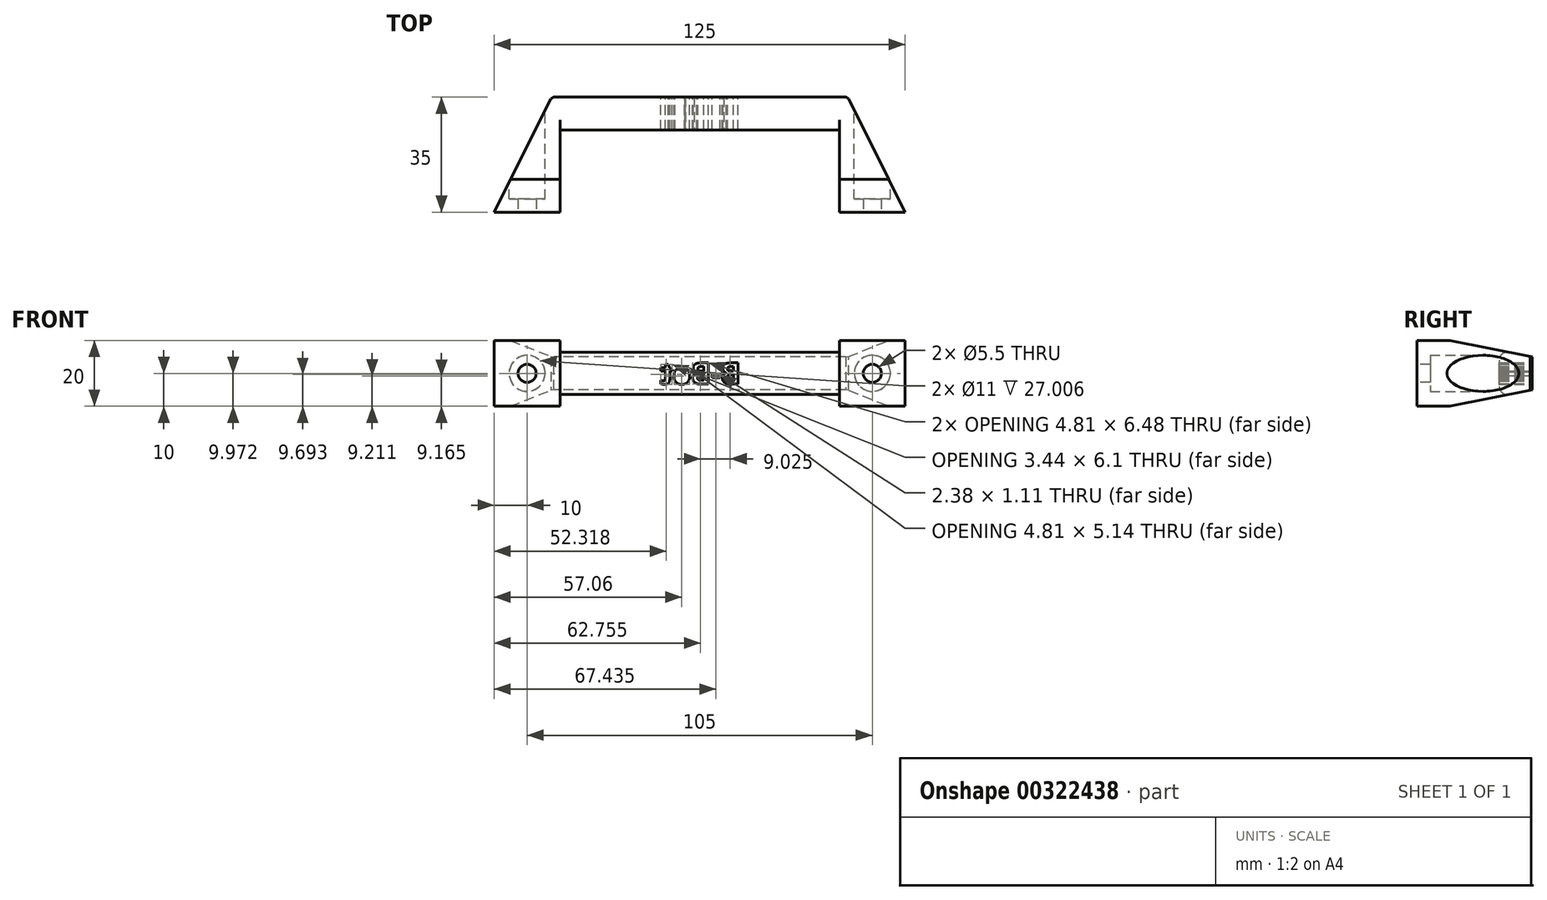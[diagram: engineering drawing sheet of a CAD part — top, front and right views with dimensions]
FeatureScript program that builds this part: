
annotation { "Feature Type Name" : "Feature", "Feature Type Description" : "" }
export const myFeature = defineFeature(function(context is Context, id is Id, definition is map)
    precondition{}
    {
        {
            var Q0;
            Q0=qCreatedBy(makeId("Top.planeOp"),FACE);
            var sketch = newSketch(context, id + "F0", { "sketchPlane" : qUnion([Q0])});
            skLineSegment(sketch, "E0", {"start": v(0, 0) * mm, "end": v(-20, 0) * mm});
            skLineSegment(sketch, "E1", {"start": v(0, 0) * mm, "end": v(0, 25) * mm});
            skLineSegment(sketch, "E2", {"start": v(0, 25) * mm, "end": v(85, 25) * mm});
            skLineSegment(sketch, "E3", {"start": v(85, 25) * mm, "end": v(85, 0) * mm});
            skLineSegment(sketch, "E4", {"start": v(85, 0) * mm, "end": v(105, 0) * mm});
            skLineSegment(sketch, "E5", {"start": v(105, 0) * mm, "end": v(87.5, 35) * mm});
            skLineSegment(sketch, "E6", {"start": v(87.5, 35) * mm, "end": v(-2.5, 35) * mm});
            skLineSegment(sketch, "E7", {"start": v(-2.5, 35) * mm, "end": v(-20, 0) * mm});
            skSolve(sketch);
        }
        {
            var Q0;
            Q0=makeQuery(id+"F0.imprint","IMPRINT",FACE,{"disambiguationData":[TD([[makeQuery(id+"F0.imprint","IMPRINT",EDGE,{"derivedFrom":sQuery(id+"F0.wireOp",EDGE,"E0")}),-1.0]])]});
            extrude(context, id + "F1", {"entities" : qUnion([Q0]), "depth" : 20 * mm});
        }
        {
            var Q0;
            Q0=qCreatedBy(makeId("Right.planeOp"),FACE);
            cPlane(context, id + "F2", {"entities" : qUnion([Q0]), "cplaneType" : CPlaneType.OFFSET, "offset" : 20 * mm, "oppositeDirection" : true, "width" : 150 * mm, "height" : 150 * mm});
        }
        {
            var Q0;
            Q0=qCreatedBy(id+"F2.planeOp",FACE);
            var sketch = newSketch(context, id + "F3", { "sketchPlane" : qUnion([Q0])});
            skLineSegment(sketch, "E8.0.0", {"start": v(35, 0) * mm, "end": v(0, 0) * mm, "construction": true});
            skLineSegment(sketch, "E8.0.1", {"start": v(0, 0) * mm, "end": v(0, 20) * mm, "construction": true});
            skLineSegment(sketch, "E8.0.2", {"start": v(0, 20) * mm, "end": v(35, 20) * mm, "construction": true});
            skLineSegment(sketch, "E8.0.3", {"start": v(35, 20) * mm, "end": v(35, 0) * mm, "construction": true});
            skLineSegment(sketch, "E9.0.1", {"start": v(25, 0) * mm, "end": v(25, 20) * mm, "construction": true});
            skLineSegment(sketch, "E9.0.3", {"start": v(25, 20) * mm, "end": v(25, 0) * mm, "construction": true});
            skLineSegment(sketch, "E10", {"start": v(35, 5) * mm, "end": v(10, 0) * mm});
            skLineSegment(sketch, "E11", {"start": v(10, 0) * mm, "end": v(35, 0) * mm});
            skLineSegment(sketch, "E12", {"start": v(35, 0) * mm, "end": v(35, 5) * mm});
            skLineSegment(sketch, "E13", {"start": v(35, 10) * mm, "end": v(0, 10) * mm, "construction": true});
            skLineSegment(sketch, "E14.MirrorCS", {"start": v(10, 20) * mm, "end": v(35, 20) * mm});
            skLineSegment(sketch, "E15.MirrorCS", {"start": v(35, 15) * mm, "end": v(10, 20) * mm});
            skLineSegment(sketch, "E16.MirrorCS", {"start": v(35, 20) * mm, "end": v(35, 15) * mm});
            skSolve(sketch);
        }
        {
            var Q0;
            Q0 = qSketchRegion(id + "F3", true);
            extrude(context, id + "F4", {"entities" : qUnion([Q0]), "operationType" : NewBodyOperationType.REMOVE, "endBound" : BoundingType.THROUGH_ALL, "depth" : 25 * mm});
        }
        {
            var Q0;
            Q0=makeQuery(id+"F1.opExtrude","SWEPT_FACE",FACE,{"disambiguationData":[OSD([sQuery(id+"F0.wireOp",EDGE,"E6")])]});
            var sketch = newSketch(context, id + "F5", { "sketchPlane" : qUnion([Q0])});
            skLineSegment(sketch, "E17.0.0", {"start": v(-87.5, 15) * mm, "end": v(-87.5, 5) * mm, "construction": true});
            skLineSegment(sketch, "E17.0.1", {"start": v(-87.5, 5) * mm, "end": v(2.5, 5) * mm, "construction": true});
            skLineSegment(sketch, "E17.0.2", {"start": v(2.5, 5) * mm, "end": v(2.5, 15) * mm, "construction": true});
            skLineSegment(sketch, "E17.0.3", {"start": v(2.5, 15) * mm, "end": v(-87.5, 15) * mm, "construction": true});
            skText(sketch, "E18", { "text": "B-Bot", "fontName": "OpenSans-Bold.ttf"});
            const initialGuessF5  = {"E18": [-0.055, 0.00673, 1, 0, 0.00654]};
            skSetInitialGuess(sketch, initialGuessF5);
            skSolve(sketch);
        }
        {
            var Q0;
            Q0 = qSketchRegion(id + "F5", true);
            extrude(context, id + "F6", {"entities" : qUnion([Q0]), "operationType" : NewBodyOperationType.REMOVE, "endBound" : BoundingType.THROUGH_ALL, "oppositeDirection" : true, "depth" : 25 * mm});
        }
        {
            var Q0;
            Q0=makeQuery(id+"F6.boolean.opBoolean","SPLIT",FACE,{"disambiguationData":[TD([makeQuery(id+"F1.opExtrude","SWEPT_FACE",FACE,{"disambiguationData":[OSD([sQuery(id+"F0.wireOp",EDGE,"E5")])]})])],"derivedFrom":makeQuery(id+"F1.opExtrude","SWEPT_FACE",FACE,{"disambiguationData":[OSD([sQuery(id+"F0.wireOp",EDGE,"E6")])]})});
            var sketch = newSketch(context, id + "F7", { "sketchPlane" : qUnion([Q0])});
            skLineSegment(sketch, "E19.0.0", {"start": v(-50.3, 12.09) * mm, "end": v(-50.3, 10.65) * mm});
            skLineSegment(sketch, "E19.0.1", {"start": v(-50.3, 10.65) * mm, "end": v(-49.51, 10.65) * mm});
            skFitSpline(sketch, "E19.0.2", {"points": [v(-52.01, 10.65) * mm, v(-51.45, 10.65) * mm, v(-51.2, 10.82) * mm]});
            skFitSpline(sketch, "E19.0.3", {"points": [v(-51.2, 10.82) * mm, v(-50.95, 11) * mm, v(-50.95, 11.4) * mm]});
            skFitSpline(sketch, "E19.0.4", {"points": [v(-50.95, 11.4) * mm, v(-50.95, 11.76) * mm, v(-51.22, 11.93) * mm]});
            skFitSpline(sketch, "E19.0.5", {"points": [v(-51.22, 11.93) * mm, v(-51.5, 12.09) * mm, v(-52.09, 12.09) * mm]});
            skLineSegment(sketch, "E19.0.6", {"start": v(-49.59, 12.09) * mm, "end": v(-50.3, 12.09) * mm});
            skLineSegment(sketch, "E20.0.0", {"start": v(-49.46, 9.56) * mm, "end": v(-50.3, 9.56) * mm});
            skLineSegment(sketch, "E20.0.1", {"start": v(-50.3, 9.56) * mm, "end": v(-50.3, 7.86) * mm});
            skLineSegment(sketch, "E20.0.2", {"start": v(-50.3, 7.86) * mm, "end": v(-49.41, 7.86) * mm});
            skFitSpline(sketch, "E20.0.3", {"points": [v(-51.91, 7.86) * mm, v(-51.34, 7.86) * mm, v(-51.07, 8.08) * mm]});
            skFitSpline(sketch, "E20.0.4", {"points": [v(-51.07, 8.08) * mm, v(-50.8, 8.3) * mm, v(-50.8, 8.75) * mm]});
            skFitSpline(sketch, "E20.0.5", {"points": [v(-50.8, 8.75) * mm, v(-50.8, 9.56) * mm, v(-51.96, 9.56) * mm]});
            skLineSegment(sketch, "E21.0.0", {"start": v(-41.28, 12.09) * mm, "end": v(-41.28, 10.65) * mm});
            skLineSegment(sketch, "E21.0.1", {"start": v(-41.28, 10.65) * mm, "end": v(-40.48, 10.65) * mm});
            skFitSpline(sketch, "E21.0.2", {"points": [v(-42.98, 10.65) * mm, v(-42.42, 10.65) * mm, v(-42.17, 10.82) * mm]});
            skFitSpline(sketch, "E21.0.3", {"points": [v(-42.17, 10.82) * mm, v(-41.92, 11) * mm, v(-41.92, 11.4) * mm]});
            skFitSpline(sketch, "E21.0.4", {"points": [v(-41.92, 11.4) * mm, v(-41.92, 11.76) * mm, v(-42.2, 11.93) * mm]});
            skFitSpline(sketch, "E21.0.5", {"points": [v(-42.2, 11.93) * mm, v(-42.47, 12.09) * mm, v(-43.06, 12.09) * mm]});
            skLineSegment(sketch, "E21.0.6", {"start": v(-40.56, 12.09) * mm, "end": v(-41.28, 12.09) * mm});
            skLineSegment(sketch, "E22.0.0", {"start": v(-40.43, 9.56) * mm, "end": v(-41.28, 9.56) * mm});
            skLineSegment(sketch, "E22.0.1", {"start": v(-41.28, 9.56) * mm, "end": v(-41.28, 7.86) * mm});
            skLineSegment(sketch, "E22.0.2", {"start": v(-41.28, 7.86) * mm, "end": v(-40.38, 7.86) * mm});
            skFitSpline(sketch, "E22.0.3", {"points": [v(-42.88, 7.86) * mm, v(-42.32, 7.86) * mm, v(-42.05, 8.08) * mm]});
            skFitSpline(sketch, "E22.0.4", {"points": [v(-42.05, 8.08) * mm, v(-41.78, 8.3) * mm, v(-41.78, 8.75) * mm]});
            skFitSpline(sketch, "E22.0.5", {"points": [v(-41.78, 8.75) * mm, v(-41.78, 9.56) * mm, v(-42.93, 9.56) * mm]});
            skFitSpline(sketch, "E23.0.0", {"points": [v(-37.84, 10.33) * mm, v(-38.08, 9.96) * mm, v(-38.08, 9.22) * mm]});
            skFitSpline(sketch, "E23.0.1", {"points": [v(-38.08, 9.22) * mm, v(-38.08, 8.48) * mm, v(-37.84, 8.1) * mm]});
            skFitSpline(sketch, "E23.0.2", {"points": [v(-37.84, 8.1) * mm, v(-37.6, 7.73) * mm, v(-37.05, 7.73) * mm]});
            skFitSpline(sketch, "E23.0.3", {"points": [v(-37.05, 7.73) * mm, v(-36.5, 7.73) * mm, v(-36.27, 8.1) * mm]});
            skFitSpline(sketch, "E23.0.4", {"points": [v(-36.27, 8.1) * mm, v(-36.03, 8.48) * mm, v(-36.03, 9.22) * mm]});
            skFitSpline(sketch, "E23.0.5", {"points": [v(-36.03, 9.22) * mm, v(-36.03, 9.95) * mm, v(-36.27, 10.32) * mm]});
            skFitSpline(sketch, "E23.0.6", {"points": [v(-36.27, 10.32) * mm, v(-36.51, 10.7) * mm, v(-37.06, 10.7) * mm]});
            skFitSpline(sketch, "E23.0.7", {"points": [v(-37.06, 10.7) * mm, v(-37.6, 10.7) * mm, v(-37.84, 10.33) * mm]});
            skSolve(sketch);
        }
        {
            var Q0;
            Q0 = qSketchRegion(id + "F7", true);
            extrude(context, id + "F8", {"entities" : qUnion([Q0]), "operationType" : NewBodyOperationType.REMOVE, "endBound" : BoundingType.THROUGH_ALL, "oppositeDirection" : true, "depth" : 25 * mm});
        }
        {
            var Q0;
            Q0=makeQuery(id+"F4.boolean.opBoolean","COPY",EDGE,{"derivedFrom":makeQuery(id+"F4.opExtrude","SWEPT_EDGE",EDGE,{"disambiguationData":[OSD([sQuery(id+"F3.wireOp",EDGE,"E10"),sQuery(id+"F3.wireOp",EDGE,"E12")])]})});
            var Q1;
            Q1=makeQuery(id+"F4.boolean.opBoolean","COPY",EDGE,{"derivedFrom":makeQuery(id+"F4.opExtrude","SWEPT_EDGE",EDGE,{"disambiguationData":[OSD([sQuery(id+"F3.wireOp",EDGE,"E15.MirrorCS"),sQuery(id+"F3.wireOp",EDGE,"E16.MirrorCS")])]})});
            var Q2;
            Q2=makeQuery(id+"F1.opExtrude","SWEPT_EDGE",EDGE,{"disambiguationData":[OSD([sQuery(id+"F0.wireOp",EDGE,"E6"),sQuery(id+"F0.wireOp",EDGE,"E7")])]});
            var Q3;
            Q3=makeQuery(id+"F1.opExtrude","SWEPT_EDGE",EDGE,{"disambiguationData":[OSD([sQuery(id+"F0.wireOp",EDGE,"E5"),sQuery(id+"F0.wireOp",EDGE,"E6")])]});
            chamfer(context, id + "F9", {"entities" : qUnion([Q0, Q1, Q2, Q3]), "width" : 1 * mm, "tangentPropagation" : true});
        }
        {
            var Q0;
            Q0=makeQuery(id+"F4.boolean.opBoolean","INTERSECT",EDGE,{"derivedFrom":[makeQuery(id+"F1.opExtrude","SWEPT_FACE",FACE,{"disambiguationData":[OSD([sQuery(id+"F0.wireOp",EDGE,"E2")])]}),makeQuery(id+"F4.opExtrude","SWEPT_FACE",FACE,{"disambiguationData":[OSD([sQuery(id+"F3.wireOp",EDGE,"E15.MirrorCS")])]})]});
            var Q1;
            Q1=makeQuery(id+"F4.boolean.opBoolean","INTERSECT",EDGE,{"derivedFrom":[makeQuery(id+"F1.opExtrude","SWEPT_FACE",FACE,{"disambiguationData":[OSD([sQuery(id+"F0.wireOp",EDGE,"E2")])]}),makeQuery(id+"F4.opExtrude","SWEPT_FACE",FACE,{"disambiguationData":[OSD([sQuery(id+"F3.wireOp",EDGE,"E10")])]})]});
            fillet(context, id + "F10", {"entities" : qUnion([Q0, Q1]), "radius" : 2.5 * mm, "tangentPropagation" : true, "allowEdgeOverflow" : false});
        }
        {
            var Q0;
            Q0=makeQuery(id+"F1.opExtrude","SWEPT_FACE",FACE,{"disambiguationData":[OSD([sQuery(id+"F0.wireOp",EDGE,"E4")])]});
            var sketch = newSketch(context, id + "F11", { "sketchPlane" : qUnion([Q0])});
            skLineSegment(sketch, "E24.0.0", {"start": v(-20, 0) * mm, "end": v(0, 0) * mm, "construction": true});
            skLineSegment(sketch, "E24.0.1", {"start": v(0, 0) * mm, "end": v(0, 20) * mm, "construction": true});
            skLineSegment(sketch, "E24.0.2", {"start": v(0, 20) * mm, "end": v(-20, 20) * mm, "construction": true});
            skLineSegment(sketch, "E24.0.3", {"start": v(-20, 20) * mm, "end": v(-20, 0) * mm, "construction": true});
            skLineSegment(sketch, "E25.0.0", {"start": v(85, 0) * mm, "end": v(105, 0) * mm, "construction": true});
            skLineSegment(sketch, "E25.0.1", {"start": v(105, 0) * mm, "end": v(105, 20) * mm, "construction": true});
            skLineSegment(sketch, "E25.0.2", {"start": v(105, 20) * mm, "end": v(85, 20) * mm, "construction": true});
            skLineSegment(sketch, "E25.0.3", {"start": v(85, 20) * mm, "end": v(85, 0) * mm, "construction": true});
            skCircle(sketch, "E26", {"center": v(-10, 10) * mm, "radius": 2.75 * mm});
            skPoint(sketch, "E26.centerSnap0", {"position": v(0, 10) * mm});
            skPoint(sketch, "E26.centerSnap1", {"position": v(-10, 20) * mm});
            skCircle(sketch, "E27", {"center": v(95, 10) * mm, "radius": 2.75 * mm});
            skPoint(sketch, "E27.centerSnap0", {"position": v(85, 10) * mm});
            skPoint(sketch, "E27.centerSnap1", {"position": v(95, 20) * mm});
            skSolve(sketch);
        }
        {
            var Q0;
            Q0 = qSketchRegion(id + "F11", true);
            extrude(context, id + "F12", {"entities" : qUnion([Q0]), "operationType" : NewBodyOperationType.REMOVE, "endBound" : BoundingType.THROUGH_ALL, "oppositeDirection" : true, "depth" : 25 * mm});
        }
        {
            var Q0;
            Q0=makeQuery(id+"F6.boolean.opBoolean","SPLIT",FACE,{"disambiguationData":[TD([makeQuery(id+"F1.opExtrude","SWEPT_FACE",FACE,{"disambiguationData":[OSD([sQuery(id+"F0.wireOp",EDGE,"E5")])]})])],"derivedFrom":makeQuery(id+"F1.opExtrude","SWEPT_FACE",FACE,{"disambiguationData":[OSD([sQuery(id+"F0.wireOp",EDGE,"E6")])]})});
            var sketch = newSketch(context, id + "F13", { "sketchPlane" : qUnion([Q0])});
            skCircle(sketch, "E28.0", {"center": v(-95, 10) * mm, "radius": 2.75 * mm, "construction": true});
            skCircle(sketch, "E29.0", {"center": v(10, 10) * mm, "radius": 2.75 * mm, "construction": true});
            skCircle(sketch, "E30", {"center": v(-95, 10) * mm, "radius": 5.5 * mm});
            skCircle(sketch, "E31", {"center": v(10, 10) * mm, "radius": 5.5 * mm});
            skSolve(sketch);
        }
        {
            var Q0;
            Q0 = qSketchRegion(id + "F13", true);
            extrude(context, id + "F14", {"entities" : qUnion([Q0]), "operationType" : NewBodyOperationType.REMOVE, "oppositeDirection" : true, "depth" : 31 * mm});
        }
    });
